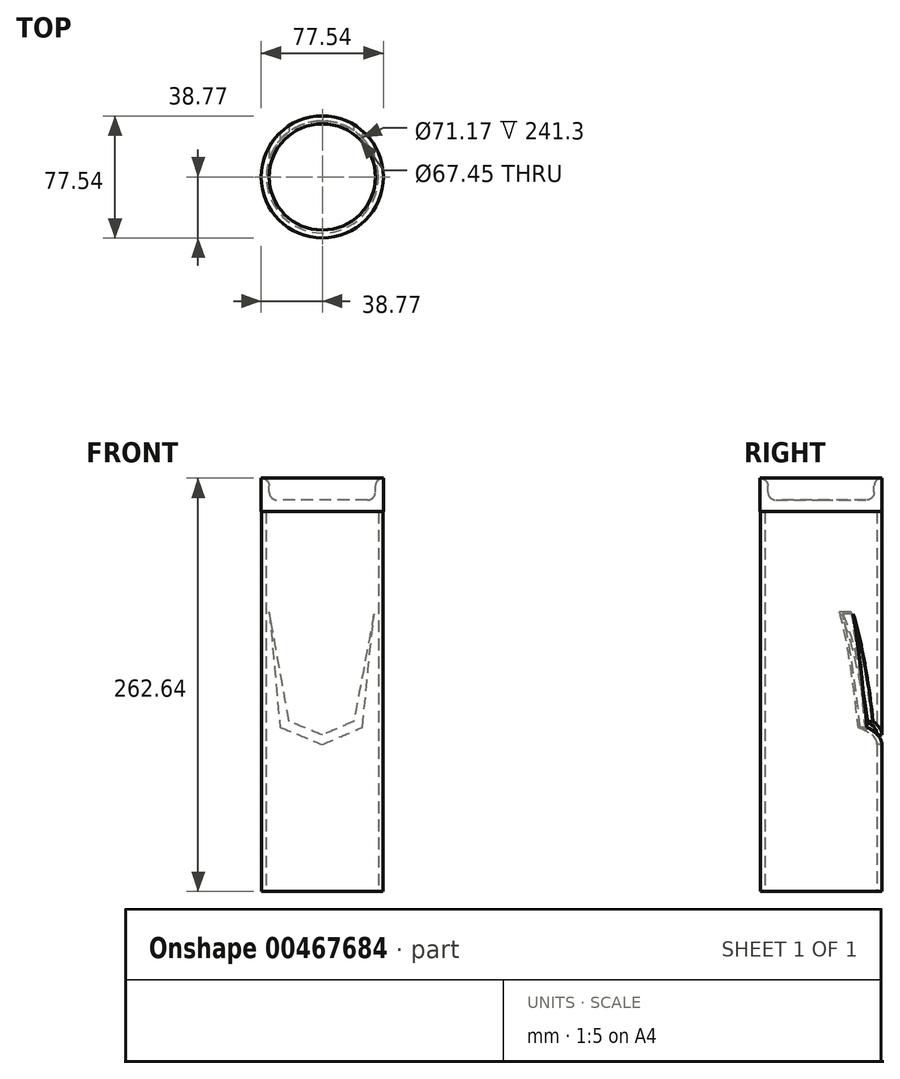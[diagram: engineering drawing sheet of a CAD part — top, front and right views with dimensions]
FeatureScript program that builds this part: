
annotation { "Feature Type Name" : "Feature", "Feature Type Description" : "" }
export const myFeature = defineFeature(function(context is Context, id is Id, definition is map)
    precondition{}
    {
        {
            var Q0;
            Q0=qCreatedBy(makeId("Top.planeOp"),FACE);
            var sketch = newSketch(context, id + "F0", { "sketchPlane" : qUnion([Q0])});
            skCircle(sketch, "E0", {"center": v(0, 0) * mm, "radius": 38.63 * mm});
            skCircle(sketch, "E1", {"center": v(0, 0) * mm, "radius": 35.58 * mm});
            skSolve(sketch);
        }
        {
            var Q0;
            Q0=makeQuery(id+"F0.imprint","IMPRINT",FACE,{"disambiguationData":[TD([[makeQuery(id+"F0.imprint","IMPRINT",EDGE,{"derivedFrom":sQuery(id+"F0.wireOp",EDGE,"E0")}),1.0]])]});
            extrude(context, id + "F1", {"entities" : qUnion([Q0]), "depth" : 241.3 * mm});
        }
        {
            var Q0;
            Q0=makeQuery(id+"F1.opExtrude","CAP_FACE",FACE,{"disambiguationData":[OSD([sQuery(id+"F0.wireOp",EDGE,"E0"),sQuery(id+"F0.wireOp",EDGE,"E1")])],"isStart":false});
            var sketch = newSketch(context, id + "F2", { "sketchPlane" : qUnion([Q0])});
            skCircle(sketch, "E2", {"center": v(0, 0) * mm, "radius": 38.77 * mm});
            skSolve(sketch);
        }
        {
            var Q0;
            Q0 = qSketchRegion(id + "F2", true);
            extrude(context, id + "F3", {"entities" : qUnion([Q0]), "operationType" : NewBodyOperationType.ADD, "depth" : 21.34 * mm});
        }
        {
            var Q0;
            Q0=makeQuery(id+"F3.opExtrude","CAP_FACE",FACE,{"disambiguationData":[OSD([sQuery(id+"F2.wireOp",EDGE,"E2")])],"isStart":false});
            var sketch = newSketch(context, id + "F4", { "sketchPlane" : qUnion([Q0])});
            skCircle(sketch, "E3", {"center": v(0, 0) * mm, "radius": 33.72 * mm});
            skSolve(sketch);
        }
        {
            var Q0;
            Q0=makeQuery(id+"F4.imprint","IMPRINT",FACE,{"disambiguationData":[TD([[makeQuery(id+"F4.imprint","IMPRINT",EDGE,{"derivedFrom":sQuery(id+"F4.wireOp",EDGE,"E3")}),1.0]])]});
            extrude(context, id + "F5", {"entities" : qUnion([Q0]), "operationType" : NewBodyOperationType.REMOVE, "oppositeDirection" : true, "depth" : 13.97 * mm});
        }
        {
            var Q0;
            Q0=makeQuery(id+"F5.boolean.opBoolean","COPY",FACE,{"derivedFrom":makeQuery(id+"F5.opExtrude","SWEPT_FACE",FACE,{"disambiguationData":[OSD([sQuery(id+"F4.wireOp",EDGE,"E3")])]})});
            fillet(context, id + "F6", {"entities" : qUnion([Q0]), "radius" : 5.08 * mm, "tangentPropagation" : true, "allowEdgeOverflow" : false});
        }
        {
            var Q0;
            Q0=qCreatedBy(makeId("Front.planeOp"),FACE);
            var sketch = newSketch(context, id + "F7", { "sketchPlane" : qUnion([Q0])});
            skLineSegment(sketch, "E4", {"start": v(-33.65, 177.67) * mm, "end": v(-26.88, 104.42) * mm});
            skLineSegment(sketch, "E5", {"start": v(-26.88, 104.42) * mm, "end": v(0, 93.34) * mm});
            skLineSegment(sketch, "E6", {"start": v(0, 93.34) * mm, "end": v(25.44, 104.42) * mm});
            skLineSegment(sketch, "E7", {"start": v(25.44, 104.42) * mm, "end": v(32.82, 176.44) * mm});
            skLineSegment(sketch, "E8", {"start": v(32.82, 176.44) * mm, "end": v(19.9, 108.11) * mm});
            skLineSegment(sketch, "E9", {"start": v(19.9, 108.11) * mm, "end": v(0, 99.45) * mm});
            skLineSegment(sketch, "E10", {"start": v(0, 99.45) * mm, "end": v(-21.03, 108.11) * mm});
            skLineSegment(sketch, "E11", {"start": v(-21.03, 108.11) * mm, "end": v(-33.65, 177.67) * mm});
            skSolve(sketch);
        }
        {
            var Q0;
            Q0 = qSketchRegion(id + "F7", true);
            extrude(context, id + "F8", {"entities" : qUnion([Q0]), "operationType" : NewBodyOperationType.REMOVE, "oppositeDirection" : true, "depth" : 59.94 * mm});
        }
    });
